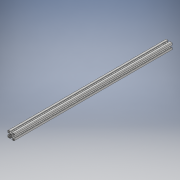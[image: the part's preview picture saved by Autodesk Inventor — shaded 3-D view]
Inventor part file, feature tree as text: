
AUTODESK INVENTOR PART (.ipt)
format: ipt  version: 2018 (Build 220112000, 112)  size: 550,912 bytes
history: native  units: in
note: dims shown in document units (in); Inventor stores cm internally (conversion verified against a paired STEP export)
features: direct_edit x1, extrude x1, plane x1, mirror x1, sketch x1, projected_geometry x1, other x1, move_body x1
ambient origin geometry x8: Origin, YZ Plane, XZ Plane, XY Plane, X Axis, Y Axis, Z Axis, Center Point
bodies: Solid1 (feature_tree)
feature tree (8):
  direct_edit  "Direct Edit1"
  extrude  "Extrusion1"  Depth=0.5312in
  plane  "Work Plane1"
  mirror  "Mirror1"
  sketch  "Sketch1"  dims[d0=0.0in d1=0.0in d2=36.0in d3=0.5312in d4=1.0in d5=1.0in d6=0.0in]
  projected_geometry  "Projected Loop1"
  other  "8020-1515-LS-1515-LS X 145_1_1:1"
  move_body  "Move1"
